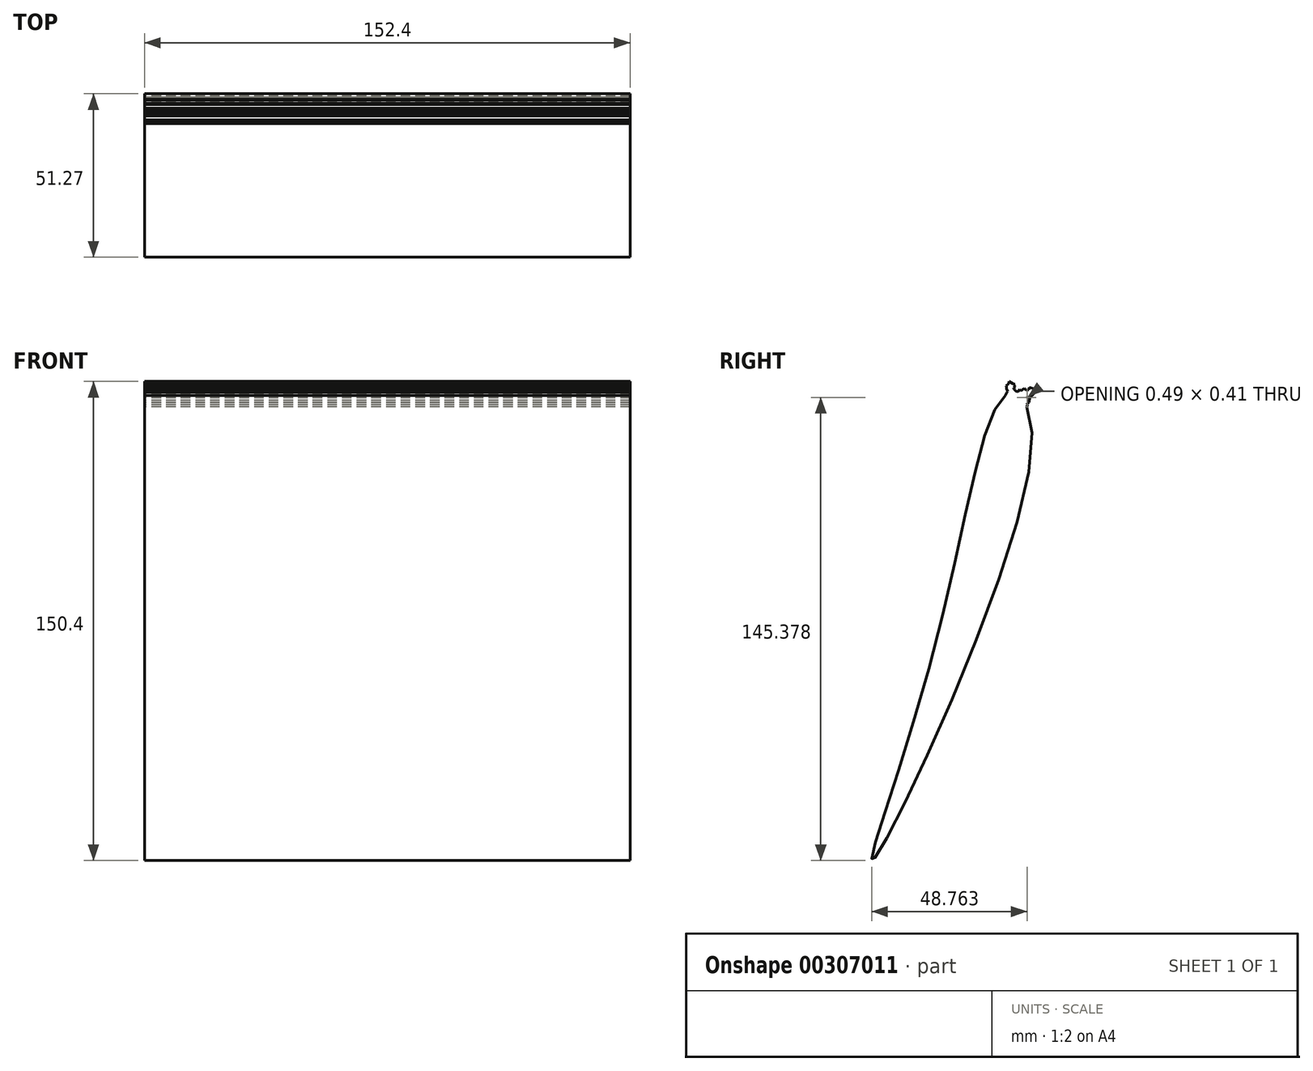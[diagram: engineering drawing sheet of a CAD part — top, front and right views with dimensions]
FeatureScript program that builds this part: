
annotation { "Feature Type Name" : "Feature", "Feature Type Description" : "" }
export const myFeature = defineFeature(function(context is Context, id is Id, definition is map)
    precondition{}
    {
        {
            var Q0;
            Q0=qCreatedBy(makeId("Right.planeOp"),FACE);
            var sketch = newSketch(context, id + "F0", { "sketchPlane" : qUnion([Q0])});
            skFitSpline(sketch, "E0", {"points": [v(39.8, 69.46) * mm, v(47.54, 53.67) * mm, v(-2.03, -76.46) * mm, v(16.63, -11.39) * mm, v(39.8, 69.46) * mm]});
            skLineSegment(sketch, "E1", {"start": v(43.86, 68.68) * mm, "end": v(46.78, 70.82) * mm});
            skLineSegment(sketch, "E2", {"start": v(46.78, 70.82) * mm, "end": v(47.6, 69.83) * mm});
            skLineSegment(sketch, "E3", {"start": v(47.6, 69.83) * mm, "end": v(44.86, 67.53) * mm});
            skLineSegment(sketch, "E4", {"start": v(44.86, 67.53) * mm, "end": v(43.86, 68.68) * mm});
            skLineSegment(sketch, "E5", {"start": v(46.78, 70.82) * mm, "end": v(47.51, 71.44) * mm});
            skPoint(sketch, "E5.endSnap0", {"position": v(47.2, 70.33) * mm});
            skLineSegment(sketch, "E6", {"start": v(47.51, 71.44) * mm, "end": v(48.28, 70.4) * mm});
            skLineSegment(sketch, "E7", {"start": v(48.28, 70.4) * mm, "end": v(47.6, 69.83) * mm});
            skLineSegment(sketch, "E8", {"start": v(41.59, 69.78) * mm, "end": v(41.27, 72.4) * mm});
            skLineSegment(sketch, "E9", {"start": v(41.27, 72.4) * mm, "end": v(39.98, 72.25) * mm});
            skLineSegment(sketch, "E10", {"start": v(39.98, 72.25) * mm, "end": v(40.3, 69.65) * mm});
            skLineSegment(sketch, "E11", {"start": v(40.3, 69.65) * mm, "end": v(41.59, 69.78) * mm});
            skLineSegment(sketch, "E12", {"start": v(45.35, 66.9) * mm, "end": v(45.75, 68.27) * mm});
            skLineSegment(sketch, "E13", {"start": v(45.75, 68.27) * mm, "end": v(46.24, 68.68) * mm});
            skLineSegment(sketch, "E14", {"start": v(46.24, 68.68) * mm, "end": v(46.16, 68.43) * mm});
            skPoint(sketch, "E14.endSnap0", {"position": v(46, 68.48) * mm});
            skLineSegment(sketch, "E15", {"start": v(46.16, 68.43) * mm, "end": v(45.75, 68.27) * mm});
            skLineSegment(sketch, "E16", {"start": v(45.55, 67.59) * mm, "end": v(46.34, 68.24) * mm});
            skLineSegment(sketch, "E17", {"start": v(46.34, 68.24) * mm, "end": v(46.53, 68.93) * mm});
            skLineSegment(sketch, "E18", {"start": v(46.53, 68.93) * mm, "end": v(46.9, 68.5) * mm});
            skLineSegment(sketch, "E19", {"start": v(46.9, 68.5) * mm, "end": v(46.34, 68.24) * mm});
            skLineSegment(sketch, "E20", {"start": v(47.23, 69.51) * mm, "end": v(48.04, 69.28) * mm});
            skLineSegment(sketch, "E21", {"start": v(48.04, 69.28) * mm, "end": v(47.6, 69.83) * mm});
            skLineSegment(sketch, "E22", {"start": v(48.28, 70.4) * mm, "end": v(48.16, 69.68) * mm});
            skLineSegment(sketch, "E23", {"start": v(48.16, 69.68) * mm, "end": v(47.38, 69.02) * mm});
            skLineSegment(sketch, "E24", {"start": v(47.38, 69.02) * mm, "end": v(46.53, 68.93) * mm});
            skLineSegment(sketch, "E25", {"start": v(47.38, 69.02) * mm, "end": v(47.29, 68.71) * mm});
            skLineSegment(sketch, "E26", {"start": v(47.29, 68.71) * mm, "end": v(46.9, 68.5) * mm});
            skLineSegment(sketch, "E27", {"start": v(48.16, 69.68) * mm, "end": v(47.6, 69.83) * mm});
            skLineSegment(sketch, "E28", {"start": v(46.9, 68.5) * mm, "end": v(46.63, 67.56) * mm});
            skLineSegment(sketch, "E29", {"start": v(46.63, 67.56) * mm, "end": v(45.55, 67.59) * mm});
            skLineSegment(sketch, "E30", {"start": v(48.28, 70.4) * mm, "end": v(48.5, 71.16) * mm});
            skLineSegment(sketch, "E31", {"start": v(48.5, 71.16) * mm, "end": v(48.02, 70.75) * mm});
            skLineSegment(sketch, "E32", {"start": v(48.02, 70.75) * mm, "end": v(48.5, 71.16) * mm});
            skLineSegment(sketch, "E33", {"start": v(48.5, 71.16) * mm, "end": v(47.51, 71.44) * mm});
            skLineSegment(sketch, "E34", {"start": v(47.51, 71.44) * mm, "end": v(46.72, 71.67) * mm});
            skLineSegment(sketch, "E35", {"start": v(46.72, 71.67) * mm, "end": v(46.5, 70.9) * mm});
            skLineSegment(sketch, "E36", {"start": v(46.5, 70.9) * mm, "end": v(45.5, 70.81) * mm});
            skLineSegment(sketch, "E37", {"start": v(45.5, 70.81) * mm, "end": v(45.08, 71.3) * mm});
            skLineSegment(sketch, "E38", {"start": v(45.08, 71.3) * mm, "end": v(44.77, 70.22) * mm});
            skLineSegment(sketch, "E39", {"start": v(44.77, 70.22) * mm, "end": v(44.65, 69.8) * mm});
            skLineSegment(sketch, "E40", {"start": v(44.65, 69.8) * mm, "end": v(43.91, 69.83) * mm});
            skLineSegment(sketch, "E41", {"start": v(43.91, 69.83) * mm, "end": v(43.66, 68.97) * mm});
            skLineSegment(sketch, "E42", {"start": v(43.66, 68.97) * mm, "end": v(43.86, 68.68) * mm});
            skLineSegment(sketch, "E43", {"start": v(45.08, 71.3) * mm, "end": v(44.03, 70.43) * mm});
            skLineSegment(sketch, "E44", {"start": v(44.03, 70.43) * mm, "end": v(43.56, 71) * mm});
            skLineSegment(sketch, "E45", {"start": v(43.56, 71) * mm, "end": v(43.1, 70.25) * mm});
            skLineSegment(sketch, "E46", {"start": v(43.1, 70.25) * mm, "end": v(42.4, 70.45) * mm});
            skLineSegment(sketch, "E47", {"start": v(42.4, 70.45) * mm, "end": v(41.8, 69.92) * mm});
            skLineSegment(sketch, "E48", {"start": v(42.4, 70.45) * mm, "end": v(41.9, 71.04) * mm});
            skLineSegment(sketch, "E49", {"start": v(41.9, 71.04) * mm, "end": v(41.51, 70.7) * mm});
            skLineSegment(sketch, "E50", {"start": v(41.51, 70.7) * mm, "end": v(41.74, 71.51) * mm});
            skLineSegment(sketch, "E51", {"start": v(41.74, 71.51) * mm, "end": v(41.33, 72.01) * mm});
            skLineSegment(sketch, "E52", {"start": v(41.33, 72.01) * mm, "end": v(41.27, 72.4) * mm});
            skLineSegment(sketch, "E53", {"start": v(41.74, 71.51) * mm, "end": v(41.94, 72.21) * mm});
            skLineSegment(sketch, "E54", {"start": v(41.94, 72.21) * mm, "end": v(41.33, 72.01) * mm});
            skLineSegment(sketch, "E55", {"start": v(41.94, 72.21) * mm, "end": v(42.36, 71.71) * mm});
            skLineSegment(sketch, "E56", {"start": v(42.36, 71.71) * mm, "end": v(41.74, 71.51) * mm});
            skLineSegment(sketch, "E57", {"start": v(41.94, 72.21) * mm, "end": v(41.84, 73.07) * mm});
            skLineSegment(sketch, "E58", {"start": v(41.84, 73.07) * mm, "end": v(41.27, 72.4) * mm});
            skLineSegment(sketch, "E59", {"start": v(41.27, 72.4) * mm, "end": v(40.8, 72.96) * mm});
            skPoint(sketch, "E59.endSnap0", {"position": v(40.63, 72.32) * mm});
            skLineSegment(sketch, "E60", {"start": v(40.8, 72.96) * mm, "end": v(39.98, 72.25) * mm});
            skLineSegment(sketch, "E61", {"start": v(39.98, 72.25) * mm, "end": v(40.34, 73.5) * mm});
            skLineSegment(sketch, "E62", {"start": v(40.34, 73.5) * mm, "end": v(41.56, 72.73) * mm});
            skLineSegment(sketch, "E63", {"start": v(41.56, 72.73) * mm, "end": v(41.84, 73.07) * mm});
            skLineSegment(sketch, "E64", {"start": v(40.12, 72.73) * mm, "end": v(39.45, 72.17) * mm});
            skLineSegment(sketch, "E65", {"start": v(39.45, 72.17) * mm, "end": v(40.18, 70.75) * mm});
            skLineSegment(sketch, "E66", {"start": v(40.18, 70.75) * mm, "end": v(39.59, 71.26) * mm});
            skLineSegment(sketch, "E67", {"start": v(39.59, 71.26) * mm, "end": v(39.53, 71.72) * mm});
            skLineSegment(sketch, "E68", {"start": v(39.53, 71.72) * mm, "end": v(39.45, 72.17) * mm});
            skLineSegment(sketch, "E69", {"start": v(40.3, 69.65) * mm, "end": v(39.8, 69.46) * mm});
            skLineSegment(sketch, "E70", {"start": v(39.8, 69.46) * mm, "end": v(39.73, 70.14) * mm});
            skLineSegment(sketch, "E71", {"start": v(39.73, 70.14) * mm, "end": v(40.23, 70.65) * mm});
            skLineSegment(sketch, "E72", {"start": v(40.23, 70.65) * mm, "end": v(39.59, 71.26) * mm});
            skLineSegment(sketch, "E73", {"start": v(39.59, 71.26) * mm, "end": v(39.98, 70.4) * mm});
            skLineSegment(sketch, "E74", {"start": v(46.63, 67.56) * mm, "end": v(46.6, 66.86) * mm});
            skLineSegment(sketch, "E75", {"start": v(46.6, 66.86) * mm, "end": v(46.08, 66.81) * mm});
            skLineSegment(sketch, "E76", {"start": v(46.08, 66.81) * mm, "end": v(46.14, 66.18) * mm});
            skLineSegment(sketch, "E77", {"start": v(46.14, 66.18) * mm, "end": v(45.95, 65.54) * mm});
            skLineSegment(sketch, "E78", {"start": v(45.95, 65.54) * mm, "end": v(45.35, 66.9) * mm});
            skLineSegment(sketch, "E79", {"start": v(39.73, 70.14) * mm, "end": v(39.18, 69.09) * mm});
            skLineSegment(sketch, "E80", {"start": v(39.18, 69.09) * mm, "end": v(39.8, 69.46) * mm});
            skLineSegment(sketch, "E81", {"start": v(41.74, 71.51) * mm, "end": v(41.9, 71.04) * mm});
            skLineSegment(sketch, "E82.0", {"start": v(39.73, 70.14) * mm, "end": v(46.34, 68.24) * mm, "construction": true});
            skLineSegment(sketch, "E83.0", {"start": v(39.53, 71.72) * mm, "end": v(48.04, 69.28) * mm, "construction": true});
            skLineSegment(sketch, "E84.0", {"start": v(39.59, 71.26) * mm, "end": v(42.4, 70.45) * mm, "construction": true});
            skLineSegment(sketch, "E85.0", {"start": v(40.18, 70.75) * mm, "end": v(47.29, 68.71) * mm, "construction": true});
            skLineSegment(sketch, "E86.0", {"start": v(39.45, 72.17) * mm, "end": v(48.16, 69.68) * mm, "construction": true});
            skLineSegment(sketch, "E87.0", {"start": v(40.34, 73.5) * mm, "end": v(48.5, 71.16) * mm, "construction": true});
            skLineSegment(sketch, "E88.0", {"start": v(40.12, 72.73) * mm, "end": v(48.28, 70.4) * mm, "construction": true});
            skLineSegment(sketch, "E89.0", {"start": v(41.33, 72.01) * mm, "end": v(47.2, 70.33) * mm, "construction": true});
            skLineSegment(sketch, "E90.0", {"start": v(46, 68.48) * mm, "end": v(46.16, 68.43) * mm, "construction": true});
            skLineSegment(sketch, "E91.0", {"start": v(44.03, 70.43) * mm, "end": v(44.77, 70.22) * mm, "construction": true});
            skLineSegment(sketch, "E92.0", {"start": v(44.65, 69.8) * mm, "end": v(47.38, 69.02) * mm, "construction": true});
            skLineSegment(sketch, "E93.0", {"start": v(40.18, 70.75) * mm, "end": v(40.8, 72.96) * mm, "construction": true});
            skLineSegment(sketch, "E94.0", {"start": v(47.38, 69.02) * mm, "end": v(47.6, 69.83) * mm, "construction": true});
            skLineSegment(sketch, "E95.0", {"start": v(39.98, 72.25) * mm, "end": v(40.12, 72.73) * mm, "construction": true});
            skLineSegment(sketch, "E96.0", {"start": v(47.2, 70.33) * mm, "end": v(47.51, 71.44) * mm, "construction": true});
            skLineSegment(sketch, "E97.0", {"start": v(45.55, 67.59) * mm, "end": v(46.72, 71.67) * mm, "construction": true});
            skLineSegment(sketch, "E98.0", {"start": v(48.04, 69.28) * mm, "end": v(48.16, 69.68) * mm, "construction": true});
            skSolve(sketch);
        }
        {
            var Q0;
            Q0=qSketchRegion(id+"F0",true);
            var Q1;
            Q1=makeQuery(id+"F0.imprint","IMPRINT",FACE,{"disambiguationData":[TD([[makeQuery(id+"F0.imprint","IMPRINT",EDGE,{"derivedFrom":sQuery(id+"F0.wireOp",EDGE,"E1")}),1.0]])]});
            var Q2;
            {var subQ3=sQuery(id+"F0.wireOp",EDGE,"E1");Q2=makeQuery(id+"F0.imprint","IMPRINT",FACE,{"disambiguationData":[TD([[makeQuery(id+"F0.imprint","IMPRINT",EDGE,{"derivedFrom":subQ3}),-1.0]])]});}
            var Q3;
            {var subQ0=sQuery(id+"F0.wireOp",EDGE,"E29");Q3=makeQuery(id+"F0.imprint","IMPRINT",FACE,{"disambiguationData":[TD([[makeQuery(id+"F0.imprint","IMPRINT",EDGE,{"derivedFrom":subQ0}),1.0]])]});}
            var Q4;
            {var subQ0=sQuery(id+"F0.wireOp",EDGE,"E78");var subQ1=sQuery(id+"F0.wireOp",EDGE,"E12");var subQ2=makeQuery(id+"F0.imprint","INTERSECT",VERTEX,{"derivedFrom":[subQ1,subQ0]});Q4=makeQuery(id+"F0.imprint","IMPRINT",FACE,{"disambiguationData":[TD([[makeQuery(id+"F0.imprint","IMPRINT",EDGE,{"disambiguationData":[TD([[subQ2,1.0]])],"derivedFrom":subQ0}),1.0]])]});}
            var Q5;
            {var subQ2=sQuery(id+"F0.wireOp",EDGE,"E8");Q5=makeQuery(id+"F0.imprint","IMPRINT",FACE,{"disambiguationData":[TD([[makeQuery(id+"F0.imprint","IMPRINT",EDGE,{"derivedFrom":subQ2}),-1.0]])]});}
            var Q6;
            {var subQ0=sQuery(id+"F0.wireOp",EDGE,"E11");Q6=makeQuery(id+"F0.imprint","IMPRINT",FACE,{"disambiguationData":[TD([[makeQuery(id+"F0.imprint","IMPRINT",EDGE,{"derivedFrom":subQ0}),1.0]])]});}
            var Q7;
            {var subQ0=sQuery(id+"F0.wireOp",EDGE,"E4");Q7=makeQuery(id+"F0.imprint","IMPRINT",FACE,{"disambiguationData":[TD([[makeQuery(id+"F0.imprint","IMPRINT",EDGE,{"derivedFrom":subQ0}),-1.0]])]});}
            var Q8;
            {var subQ0=sQuery(id+"F0.wireOp",EDGE,"E78");var subQ1=sQuery(id+"F0.wireOp",EDGE,"E0");var subQ3=makeQuery(id+"F0.imprint","INTERSECT",VERTEX,{"derivedFrom":[subQ1,subQ0]});Q8=makeQuery(id+"F0.imprint","IMPRINT",FACE,{"disambiguationData":[TD([[makeQuery(id+"F0.imprint","IMPRINT",EDGE,{"disambiguationData":[TD([[subQ3,-1.0]])],"derivedFrom":subQ1}),-1.0]])]});}
            var Q9;
            {var subQ6=sQuery(id+"F0.wireOp",EDGE,"E8");Q9=makeQuery(id+"F0.imprint","IMPRINT",FACE,{"disambiguationData":[TD([[makeQuery(id+"F0.imprint","IMPRINT",EDGE,{"derivedFrom":subQ6}),1.0]])]});}
            var Q10;
            Q10=makeQuery(id+"F0.imprint","IMPRINT",FACE,{"disambiguationData":[TD([[makeQuery(id+"F0.imprint","IMPRINT",EDGE,{"derivedFrom":sQuery(id+"F0.wireOp",EDGE,"E58")}),-1.0]])]});
            var Q11;
            {var subQ0=sQuery(id+"F0.wireOp",EDGE,"E69");Q11=makeQuery(id+"F0.imprint","IMPRINT",FACE,{"disambiguationData":[TD([[makeQuery(id+"F0.imprint","IMPRINT",EDGE,{"derivedFrom":subQ0}),-1.0]])]});}
            var Q12;
            {var subQ1=sQuery(id+"F0.wireOp",EDGE,"E70");Q12=makeQuery(id+"F0.imprint","IMPRINT",FACE,{"disambiguationData":[TD([[makeQuery(id+"F0.imprint","IMPRINT",EDGE,{"derivedFrom":subQ1}),1.0]])]});}
            var Q13;
            {var subQ0=sQuery(id+"F0.wireOp",EDGE,"E80");Q13=makeQuery(id+"F0.imprint","IMPRINT",FACE,{"disambiguationData":[TD([[makeQuery(id+"F0.imprint","IMPRINT",EDGE,{"derivedFrom":subQ0}),1.0]])]});}
            var Q14;
            {var subQ5=sQuery(id+"F0.wireOp",EDGE,"E64");Q14=makeQuery(id+"F0.imprint","IMPRINT",FACE,{"disambiguationData":[TD([[makeQuery(id+"F0.imprint","IMPRINT",EDGE,{"derivedFrom":subQ5}),1.0]])]});}
            var Q15;
            {var subQ1=sQuery(id+"F0.wireOp",EDGE,"E70");Q15=makeQuery(id+"F0.imprint","IMPRINT",FACE,{"disambiguationData":[TD([[makeQuery(id+"F0.imprint","IMPRINT",EDGE,{"derivedFrom":subQ1}),-1.0]])]});}
            var Q16;
            {var subQ0=sQuery(id+"F0.wireOp",EDGE,"E67");Q16=makeQuery(id+"F0.imprint","IMPRINT",FACE,{"disambiguationData":[TD([[makeQuery(id+"F0.imprint","IMPRINT",EDGE,{"derivedFrom":subQ0}),-1.0]])]});}
            var Q17;
            {var subQ0=sQuery(id+"F0.wireOp",EDGE,"E72");var subQ1=sQuery(id+"F0.wireOp",EDGE,"E10");var subQ2=makeQuery(id+"F0.imprint","INTERSECT",VERTEX,{"derivedFrom":[subQ1,subQ0]});Q17=makeQuery(id+"F0.imprint","IMPRINT",FACE,{"disambiguationData":[TD([[makeQuery(id+"F0.imprint","IMPRINT",EDGE,{"disambiguationData":[TD([[subQ2,-1.0]])],"derivedFrom":subQ1}),1.0]])]});}
            var Q18;
            Q18=makeQuery(id+"F0.imprint","IMPRINT",FACE,{"disambiguationData":[TD([[makeQuery(id+"F0.imprint","IMPRINT",EDGE,{"derivedFrom":sQuery(id+"F0.wireOp",EDGE,"E9")}),-1.0]])]});
            var Q19;
            Q19=makeQuery(id+"F0.imprint","IMPRINT",FACE,{"disambiguationData":[TD([[makeQuery(id+"F0.imprint","IMPRINT",EDGE,{"derivedFrom":sQuery(id+"F0.wireOp",EDGE,"E17")}),-1.0]])]});
            var Q20;
            {var subQ0=sQuery(id+"F0.wireOp",EDGE,"E65");var subQ1=sQuery(id+"F0.wireOp",EDGE,"E10");var subQ2=makeQuery(id+"F0.imprint","INTERSECT",VERTEX,{"derivedFrom":[subQ1,subQ0]});Q20=makeQuery(id+"F0.imprint","IMPRINT",FACE,{"disambiguationData":[TD([[makeQuery(id+"F0.imprint","IMPRINT",EDGE,{"disambiguationData":[TD([[subQ2,-1.0]])],"derivedFrom":subQ1}),1.0]])]});}
            var Q21;
            Q21=makeQuery(id+"F0.imprint","IMPRINT",FACE,{"disambiguationData":[TD([[makeQuery(id+"F0.imprint","IMPRINT",EDGE,{"derivedFrom":sQuery(id+"F0.wireOp",EDGE,"E18")}),1.0]])]});
            var Q22;
            Q22=makeQuery(id+"F0.imprint","IMPRINT",FACE,{"disambiguationData":[TD([[makeQuery(id+"F0.imprint","IMPRINT",EDGE,{"derivedFrom":sQuery(id+"F0.wireOp",EDGE,"E49")}),-1.0]])]});
            var Q23;
            {var subQ2=sQuery(id+"F0.wireOp",EDGE,"E32");Q23=makeQuery(id+"F0.imprint","IMPRINT",FACE,{"disambiguationData":[TD([[makeQuery(id+"F0.imprint","IMPRINT",EDGE,{"derivedFrom":subQ2}),1.0]])]});}
            var Q24;
            {var subQ0=sQuery(id+"F0.wireOp",EDGE,"E66");var subQ1=sQuery(id+"F0.wireOp",EDGE,"E10");var subQ2=makeQuery(id+"F0.imprint","INTERSECT",VERTEX,{"derivedFrom":[subQ1,subQ0]});Q24=makeQuery(id+"F0.imprint","IMPRINT",FACE,{"disambiguationData":[TD([[makeQuery(id+"F0.imprint","IMPRINT",EDGE,{"disambiguationData":[TD([[subQ2,-1.0]])],"derivedFrom":subQ1}),-1.0]])]});}
            var Q25;
            Q25=makeQuery(id+"F0.imprint","IMPRINT",FACE,{"disambiguationData":[TD([[makeQuery(id+"F0.imprint","IMPRINT",EDGE,{"derivedFrom":sQuery(id+"F0.wireOp",EDGE,"E2")}),1.0]])]});
            var Q26;
            {var subQ5=sQuery(id+"F0.wireOp",EDGE,"E73");Q26=makeQuery(id+"F0.imprint","IMPRINT",FACE,{"disambiguationData":[TD([[makeQuery(id+"F0.imprint","IMPRINT",EDGE,{"derivedFrom":subQ5}),1.0]])]});}
            var Q27;
            {var subQ1=sQuery(id+"F0.wireOp",EDGE,"E14");Q27=makeQuery(id+"F0.imprint","IMPRINT",FACE,{"disambiguationData":[TD([[makeQuery(id+"F0.imprint","IMPRINT",EDGE,{"derivedFrom":subQ1}),1.0]])]});}
            var Q28;
            Q28=makeQuery(id+"F0.imprint","IMPRINT",FACE,{"disambiguationData":[TD([[makeQuery(id+"F0.imprint","IMPRINT",EDGE,{"derivedFrom":sQuery(id+"F0.wireOp",EDGE,"E16")}),-1.0]])]});
            var Q29;
            {var subQ0=sQuery(id+"F0.wireOp",EDGE,"E24");Q29=makeQuery(id+"F0.imprint","IMPRINT",FACE,{"disambiguationData":[TD([[makeQuery(id+"F0.imprint","IMPRINT",EDGE,{"derivedFrom":subQ0}),-1.0]])]});}
            var Q30;
            Q30=makeQuery(id+"F0.imprint","IMPRINT",FACE,{"disambiguationData":[TD([[makeQuery(id+"F0.imprint","IMPRINT",EDGE,{"derivedFrom":sQuery(id+"F0.wireOp",EDGE,"E13")}),-1.0]])]});
            var Q31;
            {var subQ0=sQuery(id+"F0.wireOp",EDGE,"E21");var subQ1=sQuery(id+"F0.wireOp",EDGE,"E20");var subQ2=makeQuery(id+"F0.imprint","INTERSECT",VERTEX,{"derivedFrom":[subQ1,subQ0]});Q31=makeQuery(id+"F0.imprint","IMPRINT",FACE,{"disambiguationData":[TD([[makeQuery(id+"F0.imprint","IMPRINT",EDGE,{"disambiguationData":[TD([[subQ2,1.0]])],"derivedFrom":subQ1}),1.0]])]});}
            var Q32;
            Q32=makeQuery(id+"F0.imprint","IMPRINT",FACE,{"disambiguationData":[TD([[makeQuery(id+"F0.imprint","IMPRINT",EDGE,{"derivedFrom":sQuery(id+"F0.wireOp",EDGE,"E53")}),-1.0]])]});
            var Q33;
            {var subQ0=sQuery(id+"F0.wireOp",EDGE,"E30");Q33=makeQuery(id+"F0.imprint","IMPRINT",FACE,{"disambiguationData":[TD([[makeQuery(id+"F0.imprint","IMPRINT",EDGE,{"derivedFrom":subQ0}),1.0]])]});}
            var Q34;
            Q34=makeQuery(id+"F0.imprint","IMPRINT",FACE,{"disambiguationData":[TD([[makeQuery(id+"F0.imprint","IMPRINT",EDGE,{"derivedFrom":sQuery(id+"F0.wireOp",EDGE,"E7")}),1.0]])]});
            var Q35;
            Q35=makeQuery(id+"F0.imprint","IMPRINT",FACE,{"disambiguationData":[TD([[makeQuery(id+"F0.imprint","IMPRINT",EDGE,{"derivedFrom":sQuery(id+"F0.wireOp",EDGE,"E51")}),-1.0]])]});
            var Q36;
            Q36=makeQuery(id+"F0.imprint","IMPRINT",FACE,{"disambiguationData":[TD([[makeQuery(id+"F0.imprint","IMPRINT",EDGE,{"derivedFrom":sQuery(id+"F0.wireOp",EDGE,"E52")}),-1.0]])]});
            var Q37;
            {var subQ1=sQuery(id+"F0.wireOp",EDGE,"E3");var subQ3=sQuery(id+"F0.wireOp",EDGE,"E20");var subQ4=makeQuery(id+"F0.imprint","INTERSECT",VERTEX,{"derivedFrom":[subQ1,subQ3]});Q37=makeQuery(id+"F0.imprint","IMPRINT",FACE,{"disambiguationData":[TD([[makeQuery(id+"F0.imprint","IMPRINT",EDGE,{"disambiguationData":[TD([[subQ4,-1.0]])],"derivedFrom":subQ3}),1.0]])]});}
            var Q38;
            {var subQ0=sQuery(id+"F0.wireOp",EDGE,"E27");Q38=makeQuery(id+"F0.imprint","IMPRINT",FACE,{"disambiguationData":[TD([[makeQuery(id+"F0.imprint","IMPRINT",EDGE,{"derivedFrom":subQ0}),1.0]])]});}
            var Q39;
            {var subQ4=sQuery(id+"F0.wireOp",EDGE,"E4");Q39=makeQuery(id+"F0.imprint","IMPRINT",FACE,{"disambiguationData":[TD([[makeQuery(id+"F0.imprint","IMPRINT",EDGE,{"derivedFrom":subQ4}),1.0]])]});}
            extrude(context, id + "F1", {"entities" : qUnion([Q0, Q1, Q2, Q3, Q4, Q5, Q6, Q7, Q8, Q9, Q10, Q11, Q12, Q13, Q14, Q15, Q16, Q17, Q18, Q19, Q20, Q21, Q22, Q23, Q24, Q25, Q26, Q27, Q28, Q29, Q30, Q31, Q32, Q33, Q34, Q35, Q36, Q37, Q38, Q39]), "depth" : 76.2 * mm, "hasSecondDirection" : true, "secondDirectionOppositeDirection" : true, "secondDirectionDepth" : 76.2 * mm});
        }
    });
